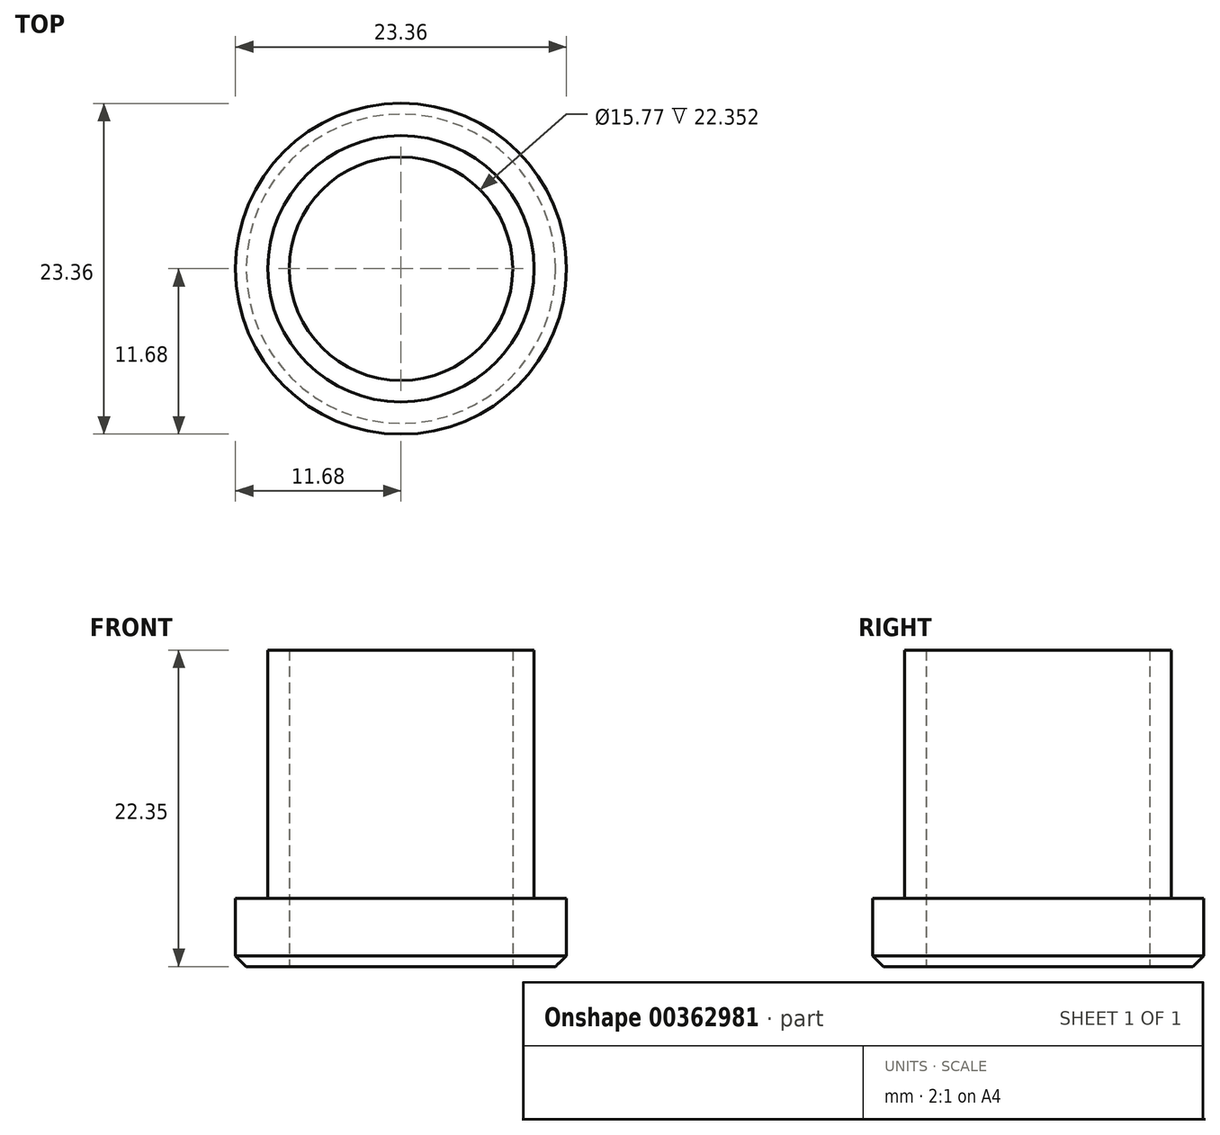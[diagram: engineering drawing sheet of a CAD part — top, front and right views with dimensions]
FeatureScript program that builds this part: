
annotation { "Feature Type Name" : "Feature", "Feature Type Description" : "" }
export const myFeature = defineFeature(function(context is Context, id is Id, definition is map)
    precondition{}
    {
        {
            var Q0;
            Q0=qCreatedBy(makeId("Top.planeOp"),FACE);
            var sketch = newSketch(context, id + "F0", { "sketchPlane" : qUnion([Q0])});
            skCircle(sketch, "E0", {"center": v(0, 0) * mm, "radius": 11.68 * mm});
            skCircle(sketch, "E1", {"center": v(0, 0) * mm, "radius": 7.89 * mm});
            skSolve(sketch);
        }
        {
            var Q0;
            Q0=makeQuery(id+"F0.imprint","IMPRINT",FACE,{"disambiguationData":[TD([[makeQuery(id+"F0.imprint","IMPRINT",EDGE,{"derivedFrom":sQuery(id+"F0.wireOp",EDGE,"E0")}),1.0]])]});
            extrude(context, id + "F1", {"entities" : qUnion([Q0]), "depth" : 4.83 * mm});
        }
        {
            var Q0;
            Q0=makeQuery(id+"F1.opExtrude","CAP_FACE",FACE,{"disambiguationData":[OSD([sQuery(id+"F0.wireOp",EDGE,"E0"),sQuery(id+"F0.wireOp",EDGE,"E1")])],"isStart":false});
            var sketch = newSketch(context, id + "F2", { "sketchPlane" : qUnion([Q0])});
            skCircle(sketch, "E2", {"center": v(0, 0) * mm, "radius": 9.4 * mm});
            skSolve(sketch);
        }
        {
            var Q0;
            Q0=makeQuery(id+"F2.imprint","IMPRINT",FACE,{"disambiguationData":[TD([[makeQuery(id+"F2.imprint","IMPRINT",EDGE,{"derivedFrom":sQuery(id+"F2.wireOp",EDGE,"E2")}),1.0]])]});
            extrude(context, id + "F3", {"entities" : qUnion([Q0]), "operationType" : NewBodyOperationType.ADD, "depth" : 17.53 * mm});
        }
        {
            var Q0;
            Q0=makeQuery(id+"F1.opExtrude","CAP_EDGE",EDGE,{"disambiguationData":[OSD([sQuery(id+"F0.wireOp",EDGE,"E0")])],"isStart":true});
            chamfer(context, id + "F4", {"entities" : qUnion([Q0]), "chamferType" : ChamferType.OFFSET_ANGLE, "width" : 0.76 * mm, "oppositeDirection" : false, "angle" : 45 * degree, "tangentPropagation" : true});
        }
    });
